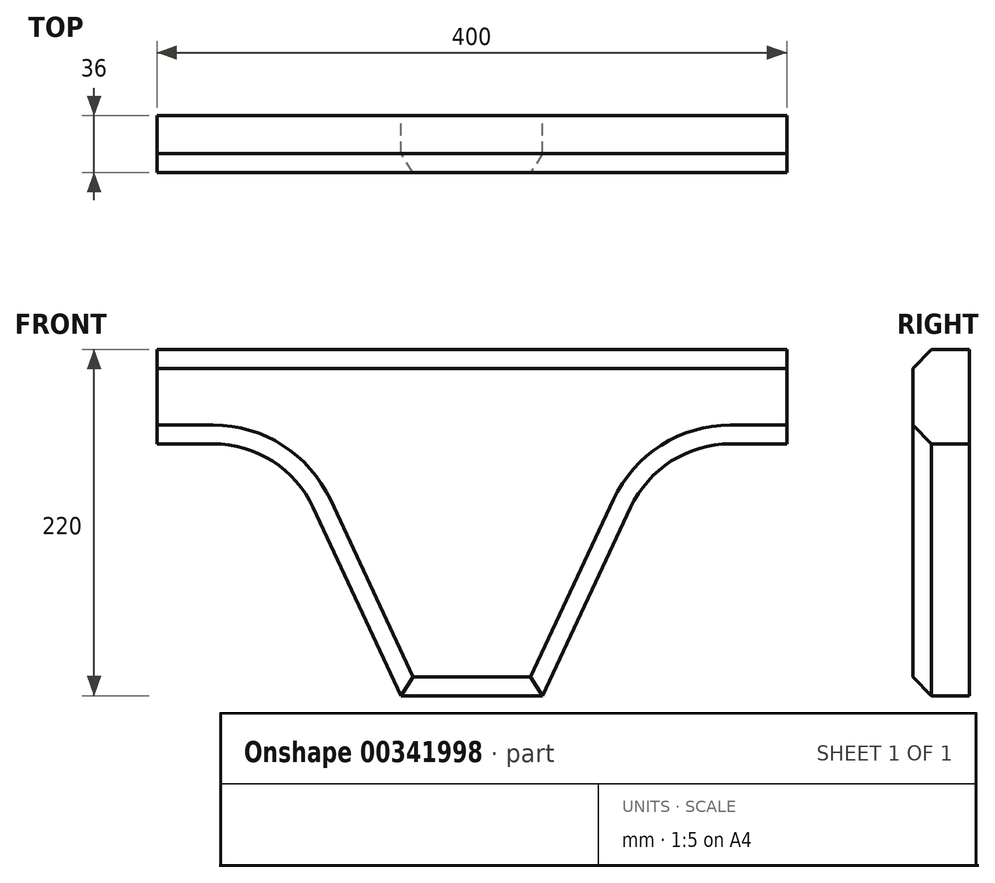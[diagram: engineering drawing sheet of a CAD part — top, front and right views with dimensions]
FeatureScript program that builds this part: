
annotation { "Feature Type Name" : "Feature", "Feature Type Description" : "" }
export const myFeature = defineFeature(function(context is Context, id is Id, definition is map)
    precondition{}
    {
        {
            var Q0;
            Q0=qCreatedBy(makeId("Front.planeOp"),FACE);
            var sketch = newSketch(context, id + "F0", { "sketchPlane" : qUnion([Q0])});
            skLineSegment(sketch, "E0", {"start": v(-45, -158.33) * mm, "end": v(45, -158.33) * mm});
            skLineSegment(sketch, "E1", {"start": v(-200, 61.67) * mm, "end": v(200, 61.67) * mm});
            skLineSegment(sketch, "E2.0", {"start": v(-200, 1.67) * mm, "end": v(-119.6, 1.67) * mm});
            skLineSegment(sketch, "E3.trimOffspring", {"start": v(119.6, 1.67) * mm, "end": v(200, 1.67) * mm});
            skLineSegment(sketch, "E4", {"start": v(-200, 61.67) * mm, "end": v(-200, 1.67) * mm});
            skLineSegment(sketch, "E5", {"start": v(200, 61.67) * mm, "end": v(200, 1.67) * mm});
            skPoint(sketch, "E6.orphan", {"position": v(-90, 31.67) * mm});
            skPoint(sketch, "E7.orphan", {"position": v(90, 31.67) * mm});
            skLineSegment(sketch, "E8", {"start": v(45, -158.33) * mm, "end": v(119.6, 1.67) * mm});
            skLineSegment(sketch, "E9", {"start": v(-45, -158.33) * mm, "end": v(-119.6, 1.67) * mm});
            skPoint(sketch, "E10.start.orphan", {"position": v(-67.5, -63.33) * mm});
            skPoint(sketch, "E11.orphan", {"position": v(67.5, -63.33) * mm});
            skSolve(sketch);
        }
        {
            var Q0;
            Q0=makeQuery(id+"F0.imprint","IMPRINT",FACE,{"disambiguationData":[TD([[makeQuery(id+"F0.imprint","IMPRINT",EDGE,{"derivedFrom":sQuery(id+"F0.wireOp",EDGE,"E0")}),1.0]])]});
            extrude(context, id + "F1", {"entities" : qUnion([Q0]), "depth" : 36 * mm});
        }
        {
            var Q0;
            Q0=makeQuery(id+"F1.opExtrude","SWEPT_EDGE",EDGE,{"disambiguationData":[OSD([sQuery(id+"F0.wireOp",EDGE,"E3.trimOffspring"),sQuery(id+"F0.wireOp",EDGE,"E8")])]});
            var Q1;
            Q1=makeQuery(id+"F1.opExtrude","SWEPT_EDGE",EDGE,{"disambiguationData":[OSD([sQuery(id+"F0.wireOp",EDGE,"E2.0"),sQuery(id+"F0.wireOp",EDGE,"E9")])]});
            fillet(context, id + "F2", {"entities" : qUnion([Q0, Q1]), "radius" : 70 * mm, "tangentPropagation" : true, "allowEdgeOverflow" : false});
        }
        {
            var Q0;
            Q0=makeQuery(id+"F1.opExtrude","CAP_EDGE",EDGE,{"disambiguationData":[OSD([sQuery(id+"F0.wireOp",EDGE,"E1")])],"isStart":false});
            var Q1;
            Q1=makeQuery(id+"F1.opExtrude","CAP_EDGE",EDGE,{"disambiguationData":[OSD([sQuery(id+"F0.wireOp",EDGE,"E3.trimOffspring")])],"isStart":false});
            var Q2;
            Q2=makeQuery(id+"F1.opExtrude","CAP_EDGE",EDGE,{"disambiguationData":[OSD([sQuery(id+"F0.wireOp",EDGE,"E9")])],"isStart":false});
            var Q3;
            Q3=makeQuery(id+"F1.opExtrude","CAP_EDGE",EDGE,{"disambiguationData":[OSD([sQuery(id+"F0.wireOp",EDGE,"E0")])],"isStart":false});
            chamfer(context, id + "F3", {"entities" : qUnion([Q0, Q1, Q2, Q3]), "width" : 12 * mm, "tangentPropagation" : true});
        }
    });
